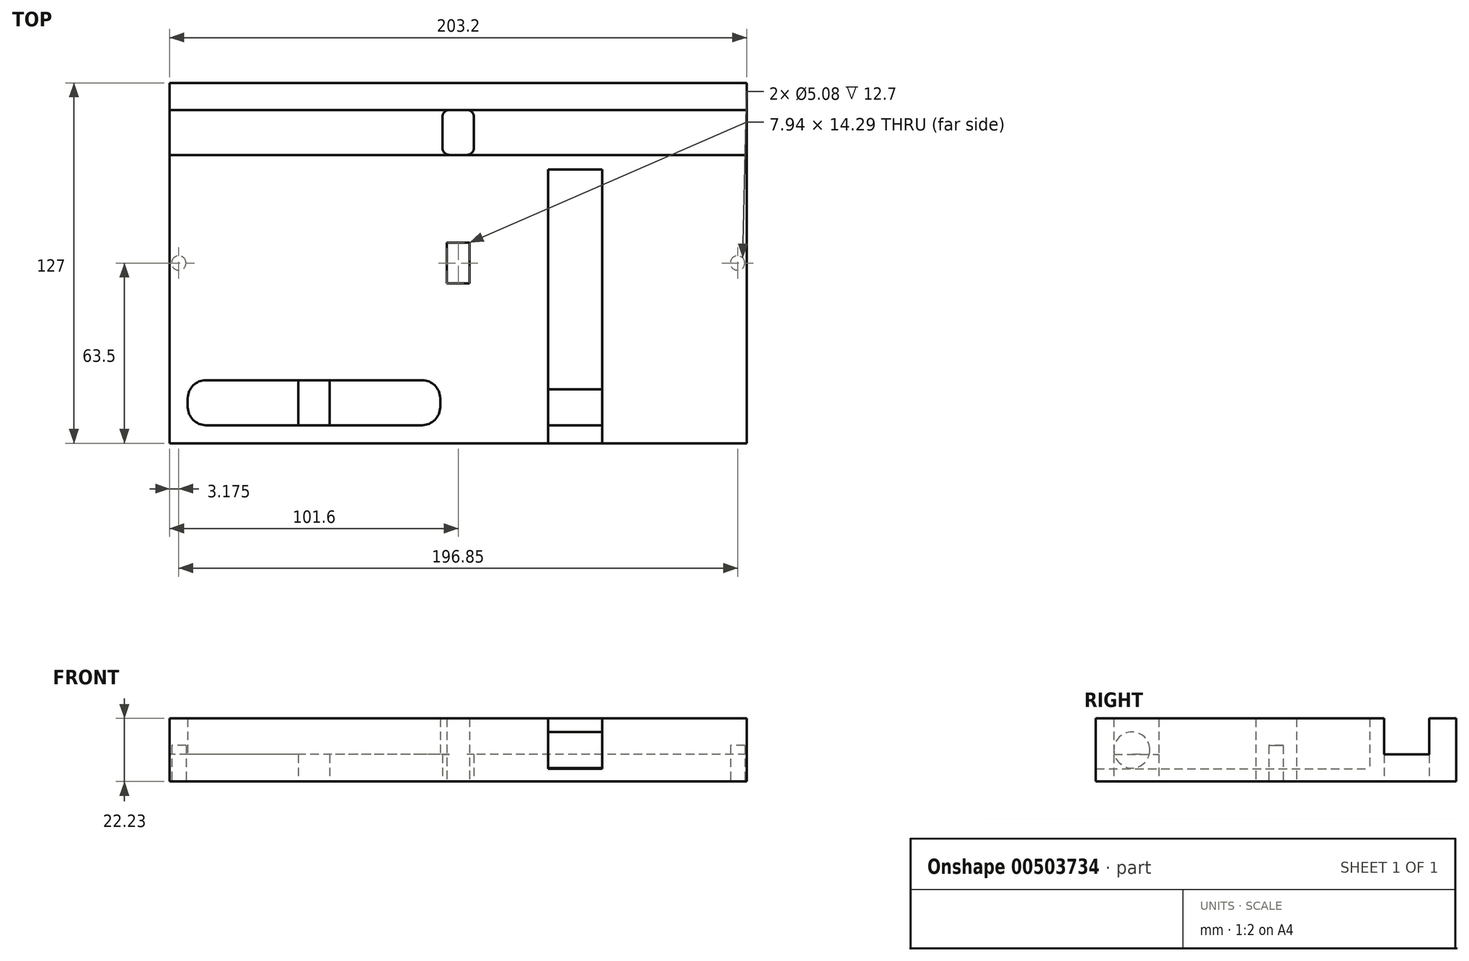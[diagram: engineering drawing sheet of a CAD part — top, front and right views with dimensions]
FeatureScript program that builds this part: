
annotation { "Feature Type Name" : "Feature", "Feature Type Description" : "" }
export const myFeature = defineFeature(function(context is Context, id is Id, definition is map)
    precondition{}
    {
        {
            var Q0;
            Q0=qCreatedBy(makeId("Top.planeOp"),FACE);
            var sketch = newSketch(context, id + "F0", { "sketchPlane" : qUnion([Q0])});
            skLineSegment(sketch, "E0.bottom", {"start": v(-101.6, -63.5) * mm, "end": v(101.6, -63.5) * mm});
            skLineSegment(sketch, "E0.top", {"start": v(-101.6, 63.5) * mm, "end": v(101.6, 63.5) * mm});
            skLineSegment(sketch, "E0.left", {"start": v(-101.6, -63.5) * mm, "end": v(-101.6, 63.5) * mm});
            skLineSegment(sketch, "E0.right", {"start": v(101.6, -63.5) * mm, "end": v(101.6, 63.5) * mm});
            skPoint(sketch, "E0.middle", {"position": v(0, 0) * mm});
            skLineSegment(sketch, "E1.bottom", {"start": v(-101.6, 53.98) * mm, "end": v(101.6, 53.98) * mm});
            skLineSegment(sketch, "E1.top", {"start": v(-101.6, 38.1) * mm, "end": v(101.6, 38.1) * mm});
            skLineSegment(sketch, "E1.left", {"start": v(-101.6, 53.98) * mm, "end": v(-101.6, 38.1) * mm});
            skLineSegment(sketch, "E1.right", {"start": v(101.6, 53.98) * mm, "end": v(101.6, 38.1) * mm});
            skLineSegment(sketch, "E2", {"start": v(-101.6, 63.5) * mm, "end": v(-101.6, 53.98) * mm});
            skPoint(sketch, "E3", {"position": v(0, 38.1) * mm});
            skPoint(sketch, "E4", {"position": v(0, 53.98) * mm});
            skLineSegment(sketch, "E5", {"start": v(0, 53.98) * mm, "end": v(0, 38.1) * mm, "construction": true});
            skPoint(sketch, "E6", {"position": v(0, 46.04) * mm});
            skLineSegment(sketch, "E7.bottom", {"start": v(-3.08, 53.98) * mm, "end": v(3.08, 53.98) * mm});
            skLineSegment(sketch, "E7.top", {"start": v(-3.08, 38.1) * mm, "end": v(3.08, 38.1) * mm});
            skLineSegment(sketch, "E7.left", {"start": v(-5.56, 51.5) * mm, "end": v(-5.56, 40.58) * mm});
            skLineSegment(sketch, "E7.right", {"start": v(5.56, 51.5) * mm, "end": v(5.56, 40.58) * mm});
            skPoint(sketch, "E8.visualSharp", {"position": v(-5.56, 53.98) * mm});
            skArc(sketch, "E8.filletArc", {"start": v(-3.08, 53.98) * mm, "mid": v(-4.83, 53.25) * mm, "end": v(-5.56, 51.5) * mm});
            skPoint(sketch, "E9.visualSharp", {"position": v(5.56, 53.98) * mm});
            skArc(sketch, "E9.filletArc", {"start": v(5.56, 51.5) * mm, "mid": v(4.83, 53.25) * mm, "end": v(3.08, 53.98) * mm});
            skPoint(sketch, "E10.visualSharp", {"position": v(5.56, 38.1) * mm});
            skArc(sketch, "E10.filletArc", {"start": v(3.08, 38.1) * mm, "mid": v(4.83, 38.83) * mm, "end": v(5.56, 40.58) * mm});
            skPoint(sketch, "E11.visualSharp", {"position": v(-5.56, 38.1) * mm});
            skArc(sketch, "E11.filletArc", {"start": v(-5.56, 40.58) * mm, "mid": v(-4.83, 38.83) * mm, "end": v(-3.08, 38.1) * mm});
            skLineSegment(sketch, "E12.bottom", {"start": v(3.97, 7.14) * mm, "end": v(-3.97, 7.14) * mm});
            skLineSegment(sketch, "E12.top", {"start": v(3.97, -7.14) * mm, "end": v(-3.97, -7.14) * mm});
            skLineSegment(sketch, "E12.left", {"start": v(3.97, 7.14) * mm, "end": v(3.97, -7.14) * mm});
            skLineSegment(sketch, "E12.right", {"start": v(-3.97, 7.14) * mm, "end": v(-3.97, -7.14) * mm});
            skPoint(sketch, "E13", {"position": v(0, 7.14) * mm});
            skPoint(sketch, "E14", {"position": v(-3.97, 0) * mm});
            skPoint(sketch, "E15", {"position": v(3.97, 0) * mm});
            skPoint(sketch, "E16", {"position": v(0, -7.14) * mm});
            skLineSegment(sketch, "E17", {"start": v(3.97, 0) * mm, "end": v(-3.97, 0) * mm, "construction": true});
            skLineSegment(sketch, "E18", {"start": v(0, 7.14) * mm, "end": v(0, -7.14) * mm, "construction": true});
            skLineSegment(sketch, "E19", {"start": v(0, 0) * mm, "end": v(-101.6, 0) * mm, "construction": true});
            skLineSegment(sketch, "E20", {"start": v(0, 0) * mm, "end": v(0, -63.5) * mm, "construction": true});
            skLineSegment(sketch, "E21", {"start": v(-101.6, -57.15) * mm, "end": v(-95.25, -57.15) * mm, "construction": true});
            skLineSegment(sketch, "E22", {"start": v(-95.25, -57.15) * mm, "end": v(-95.25, -63.5) * mm, "construction": true});
            skLineSegment(sketch, "E23.bottom", {"start": v(-88.9, -57.15) * mm, "end": v(-12.7, -57.15) * mm});
            skLineSegment(sketch, "E23.top", {"start": v(-88.9, -41.27) * mm, "end": v(-12.7, -41.27) * mm});
            skLineSegment(sketch, "E23.left", {"start": v(-95.25, -50.8) * mm, "end": v(-95.25, -47.62) * mm});
            skLineSegment(sketch, "E23.right", {"start": v(-6.35, -50.8) * mm, "end": v(-6.35, -47.62) * mm});
            skPoint(sketch, "E24.visualSharp", {"position": v(-6.35, -41.27) * mm});
            skArc(sketch, "E24.filletArc", {"start": v(-6.35, -47.62) * mm, "mid": v(-8.2, -43.13) * mm, "end": v(-12.7, -41.27) * mm});
            skPoint(sketch, "E25.visualSharp", {"position": v(-6.35, -57.15) * mm});
            skArc(sketch, "E25.filletArc", {"start": v(-12.7, -57.15) * mm, "mid": v(-8.2, -55.3) * mm, "end": v(-6.35, -50.8) * mm});
            skPoint(sketch, "E26.visualSharp", {"position": v(-95.25, -41.27) * mm});
            skArc(sketch, "E26.filletArc", {"start": v(-88.9, -41.27) * mm, "mid": v(-93.4, -43.13) * mm, "end": v(-95.25, -47.62) * mm});
            skPoint(sketch, "E27.visualSharp", {"position": v(-95.25, -57.15) * mm});
            skArc(sketch, "E27.filletArc", {"start": v(-95.25, -50.8) * mm, "mid": v(-93.4, -55.3) * mm, "end": v(-88.9, -57.15) * mm});
            skPoint(sketch, "E28", {"position": v(-50.8, -41.27) * mm});
            skPoint(sketch, "E29", {"position": v(-50.8, -57.15) * mm});
            skLineSegment(sketch, "E30", {"start": v(-50.8, -41.27) * mm, "end": v(-50.8, -57.15) * mm, "construction": true});
            skPoint(sketch, "E31", {"position": v(-95.25, -49.21) * mm});
            skPoint(sketch, "E32", {"position": v(-6.35, -49.21) * mm});
            skLineSegment(sketch, "E33", {"start": v(-95.25, -49.21) * mm, "end": v(-6.35, -49.21) * mm, "construction": true});
            skPoint(sketch, "E34", {"position": v(-50.8, -49.21) * mm});
            skLineSegment(sketch, "E35.bottom", {"start": v(-56.36, -57.15) * mm, "end": v(-45.24, -57.15) * mm});
            skLineSegment(sketch, "E35.top", {"start": v(-56.36, -41.27) * mm, "end": v(-45.24, -41.27) * mm});
            skLineSegment(sketch, "E35.left", {"start": v(-56.36, -57.15) * mm, "end": v(-56.36, -41.27) * mm});
            skLineSegment(sketch, "E35.right", {"start": v(-45.24, -57.15) * mm, "end": v(-45.24, -41.27) * mm});
            skLineSegment(sketch, "E36.bottom", {"start": v(50.8, -63.5) * mm, "end": v(31.72, -63.5) * mm});
            skLineSegment(sketch, "E36.top", {"start": v(50.8, 33.02) * mm, "end": v(31.72, 33.02) * mm});
            skLineSegment(sketch, "E36.left", {"start": v(50.8, -63.5) * mm, "end": v(50.8, 33.02) * mm});
            skLineSegment(sketch, "E36.right", {"start": v(31.72, -63.5) * mm, "end": v(31.72, 33.02) * mm});
            skLineSegment(sketch, "E37", {"start": v(50.8, -63.5) * mm, "end": v(101.6, -63.5) * mm, "construction": true});
            skSolve(sketch);
        }
        {
            var Q0;
            {var subQ5=sQuery(id+"F0.wireOp",EDGE,"E0.top");Q0=makeQuery(id+"F0.imprint","IMPRINT",FACE,{"disambiguationData":[TD([[makeQuery(id+"F0.imprint","IMPRINT",EDGE,{"derivedFrom":subQ5}),-1.0]])]});}
            var Q1;
            {Q1=qUnion([makeQuery(id+"F0.imprint","IMPRINT",FACE,{"disambiguationData":[TD([[makeQuery(id+"F0.imprint","IMPRINT",EDGE,{"derivedFrom":sQuery(id+"F0.wireOp",EDGE,"E7.left")}),-1.0]])]}),makeQuery(id+"F0.imprint","IMPRINT",FACE,{"disambiguationData":[TD([[makeQuery(id+"F0.imprint","IMPRINT",EDGE,{"derivedFrom":sQuery(id+"F0.wireOp",EDGE,"E7.right")}),1.0]])]})]);}
            var Q2;
            {Q2=qUnion([makeQuery(id+"F0.imprint","IMPRINT",FACE,{"disambiguationData":[TD([[makeQuery(id+"F0.imprint","IMPRINT",EDGE,{"derivedFrom":sQuery(id+"F0.wireOp",EDGE,"E23.left")}),-1.0]])]}),makeQuery(id+"F0.imprint","IMPRINT",FACE,{"disambiguationData":[TD([[makeQuery(id+"F0.imprint","IMPRINT",EDGE,{"derivedFrom":sQuery(id+"F0.wireOp",EDGE,"E23.right")}),1.0]])]})]);}
            var Q3;
            Q3=makeQuery(id+"F0.imprint","IMPRINT",FACE,{"disambiguationData":[TD([[makeQuery(id+"F0.imprint","IMPRINT",EDGE,{"derivedFrom":sQuery(id+"F0.wireOp",EDGE,"E12.bottom")}),-1.0]])]});
            extrude(context, id + "F1", {"entities" : qUnion([Q0, Q1, Q2, Q3]), "depth" : 9.52 * mm});
        }
        {
            var Q0;
            {var subQ5=sQuery(id+"F0.wireOp",EDGE,"E0.top");Q0=makeQuery(id+"F0.imprint","IMPRINT",FACE,{"disambiguationData":[TD([[makeQuery(id+"F0.imprint","IMPRINT",EDGE,{"derivedFrom":subQ5}),-1.0]])]});}
            var Q1;
            Q1=makeQuery(id+"F0.imprint","IMPRINT",FACE,{"disambiguationData":[TD([[makeQuery(id+"F0.imprint","IMPRINT",EDGE,{"derivedFrom":sQuery(id+"F0.wireOp",EDGE,"E12.bottom")}),-1.0]])]});
            extrude(context, id + "F2", {"entities" : qUnion([Q0, Q1]), "operationType" : NewBodyOperationType.ADD, "depth" : 22.22 * mm, "offsetDistance" : 25.4 * mm});
        }
        {
            var Q0;
            {var subQ0=sQuery(id+"F0.wireOp",EDGE,"E0.right");Q0=makeQuery(id+"F2.boolean.opBoolean","MERGE",FACE,{"derivedFrom":[makeQuery(id+"F1.opExtrude","SWEPT_FACE",FACE,{"disambiguationData":[OSD([subQ0])]}),makeQuery(id+"F2.opExtrude","SWEPT_FACE",FACE,{"disambiguationData":[OSD([subQ0]),TDD([makeQuery(id+"F0.imprint","IMPRINT",EDGE,{"disambiguationData":[TD([[makeQuery(id+"F0.imprint","INTERSECT",VERTEX,{"derivedFrom":[sQuery(id+"F0.wireOp",EDGE,"E0.bottom"),subQ0]}),-1.0]])],"derivedFrom":subQ0})])]}),makeQuery(id+"F2.opExtrude","SWEPT_FACE",FACE,{"disambiguationData":[OSD([subQ0]),TDD([makeQuery(id+"F0.imprint","IMPRINT",EDGE,{"disambiguationData":[TD([[makeQuery(id+"F0.imprint","INTERSECT",VERTEX,{"derivedFrom":[sQuery(id+"F0.wireOp",EDGE,"E0.top"),subQ0]}),1.0]])],"derivedFrom":subQ0})])]})]});}
            var sketch = newSketch(context, id + "F3", { "sketchPlane" : qUnion([Q0])});
            skPoint(sketch, "E38", {"position": v(-63.5, 11.11) * mm});
            skPoint(sketch, "E39", {"position": v(-50.8, 11.11) * mm});
            skLineSegment(sketch, "E40", {"start": v(-63.5, 11.11) * mm, "end": v(-50.8, 11.11) * mm, "construction": true});
            skCircle(sketch, "E41", {"center": v(-50.8, 11.11) * mm, "radius": 6.35 * mm});
            skSolve(sketch);
        }
        {
            var Q0;
            Q0=makeQuery(id+"F3.imprint","IMPRINT",FACE,{"disambiguationData":[TD([[makeQuery(id+"F3.imprint","IMPRINT",EDGE,{"derivedFrom":sQuery(id+"F3.wireOp",EDGE,"E41")}),1.0]])]});
            extrude(context, id + "F4", {"entities" : qUnion([Q0]), "operationType" : NewBodyOperationType.ADD, "oppositeDirection" : true, "depth" : 80.52 * mm});
        }
        {
            var Q0;
            Q0=makeQuery(id+"F0.imprint","IMPRINT",FACE,{"disambiguationData":[TD([[makeQuery(id+"F0.imprint","IMPRINT",EDGE,{"derivedFrom":sQuery(id+"F0.wireOp",EDGE,"E36.top")}),1.0]])]});
            extrude(context, id + "F5", {"entities" : qUnion([Q0]), "operationType" : NewBodyOperationType.ADD, "depth" : 4.44 * mm});
        }
        {
            var Q0;
            Q0=makeQuery(id+"F0.imprint","IMPRINT",FACE,{"disambiguationData":[TD([[makeQuery(id+"F0.imprint","IMPRINT",EDGE,{"derivedFrom":sQuery(id+"F0.wireOp",EDGE,"E12.bottom")}),-1.0]])]});
            var sketch = newSketch(context, id + "F6", { "sketchPlane" : qUnion([Q0])});
            skLineSegment(sketch, "E42", {"start": v(-101.6, 0) * mm, "end": v(101.6, 0) * mm, "construction": true});
            skLineSegment(sketch, "E43", {"start": v(-101.6, 0) * mm, "end": v(-95.25, 0) * mm, "construction": true});
            skPoint(sketch, "E44", {"position": v(-98.43, 0) * mm});
            skCircle(sketch, "E45", {"center": v(-98.43, 0) * mm, "radius": 2.54 * mm});
            skCircle(sketch, "E46.MirrorC", {"center": v(98.42, 0) * mm, "radius": 2.54 * mm});
            skSolve(sketch);
        }
        {
            var Q0;
            Q0 = qSketchRegion(id + "F6", true);
            extrude(context, id + "F7", {"entities" : qUnion([Q0]), "operationType" : NewBodyOperationType.REMOVE, "oppositeDirection" : true, "depth" : -12.7 * mm, "offsetDistance" : 25.4 * mm});
        }
    });
